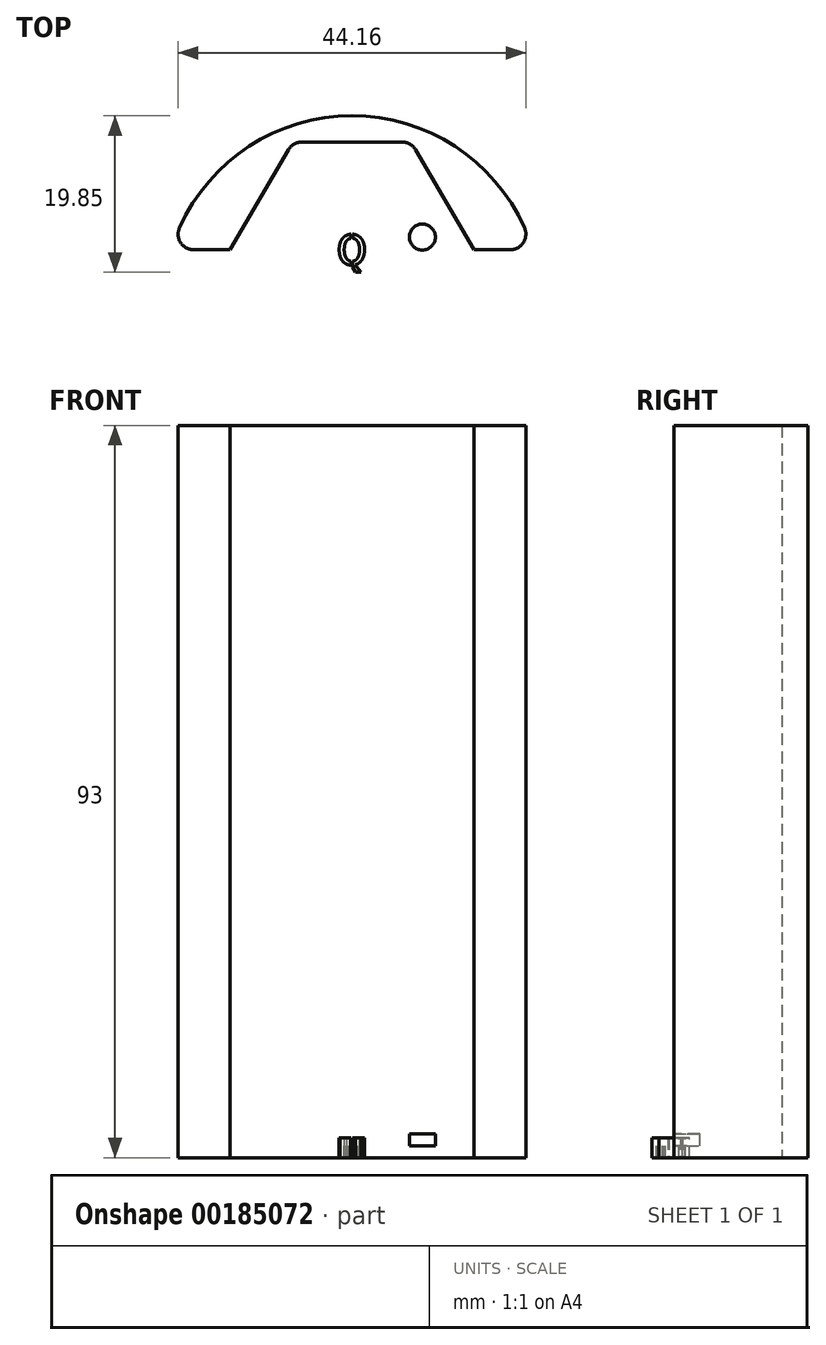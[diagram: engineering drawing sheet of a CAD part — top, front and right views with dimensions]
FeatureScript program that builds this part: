
annotation { "Feature Type Name" : "Feature", "Feature Type Description" : "" }
export const myFeature = defineFeature(function(context is Context, id is Id, definition is map)
    precondition{}
    {
        {
            var Q0;
            Q0=qCreatedBy(makeId("Top.planeOp"),FACE);
            var sketch = newSketch(context, id + "F0", { "sketchPlane" : qUnion([Q0])});
            skLineSegment(sketch, "E0", {"start": v(-15.5, -13.7) * mm, "end": v(-8.08, -1) * mm});
            skLineSegment(sketch, "E1", {"start": v(-6.35, 0) * mm, "end": v(6.35, 0) * mm});
            skLineSegment(sketch, "E2", {"start": v(8.08, -1) * mm, "end": v(15.5, -13.7) * mm});
            skLineSegment(sketch, "E3", {"start": v(-15.5, -13.7) * mm, "end": v(15.5, -13.7) * mm, "construction": true});
            skPoint(sketch, "E4", {"position": v(0, 0) * mm});
            skPoint(sketch, "E5", {"position": v(0, -13.7) * mm});
            skLineSegment(sketch, "E6", {"start": v(-15.5, -13.7) * mm, "end": v(-20.08, -13.7) * mm});
            skLineSegment(sketch, "E7", {"start": v(15.5, -13.7) * mm, "end": v(20.08, -13.7) * mm});
            skArc(sketch, "E8", {"start": v(21.9, -10.88) * mm, "mid": v(0, 3.32) * mm, "end": v(-21.9, -10.88) * mm});
            skPoint(sketch, "E9.visualSharp", {"position": v(-7.5, 0) * mm});
            skArc(sketch, "E9.filletArc", {"start": v(-6.35, 0) * mm, "mid": v(-7.35, -0.27) * mm, "end": v(-8.08, -1) * mm});
            skPoint(sketch, "E10.visualSharp", {"position": v(7.5, 0) * mm});
            skArc(sketch, "E10.filletArc", {"start": v(8.08, -1) * mm, "mid": v(7.35, -0.27) * mm, "end": v(6.35, 0) * mm});
            skPoint(sketch, "E11.visualSharp", {"position": v(-22.96, -13.7) * mm});
            skArc(sketch, "E11.filletArc", {"start": v(-21.9, -10.88) * mm, "mid": v(-21.76, -12.79) * mm, "end": v(-20.08, -13.7) * mm});
            skPoint(sketch, "E12.visualSharp", {"position": v(22.96, -13.7) * mm});
            skArc(sketch, "E12.filletArc", {"start": v(20.08, -13.7) * mm, "mid": v(21.76, -12.79) * mm, "end": v(21.9, -10.88) * mm});
            skSolve(sketch);
        }
        {
            var Q0;
            Q0=makeQuery(id+"F0.imprint","IMPRINT",FACE,{"disambiguationData":[TD([[makeQuery(id+"F0.imprint","IMPRINT",EDGE,{"derivedFrom":sQuery(id+"F0.wireOp",EDGE,"E0")}),1.0]])]});
            extrude(context, id + "F1", {"entities" : qUnion([Q0]), "depth" : 90 * mm});
        }
        {
            var Q0;
            Q0=makeQuery(id+"F1.opExtrude","CAP_FACE",FACE,{"disambiguationData":[OSD([sQuery(id+"F0.wireOp",EDGE,"E0"),sQuery(id+"F0.wireOp",EDGE,"E1"),sQuery(id+"F0.wireOp",EDGE,"E2"),sQuery(id+"F0.wireOp",EDGE,"E6"),sQuery(id+"F0.wireOp",EDGE,"E7"),sQuery(id+"F0.wireOp",EDGE,"E8"),sQuery(id+"F0.wireOp",EDGE,"E9.filletArc"),sQuery(id+"F0.wireOp",EDGE,"E10.filletArc")])],"isStart":true});
            var sketch = newSketch(context, id + "F2", { "sketchPlane" : qUnion([Q0])});
            skLineSegment(sketch, "E13", {"start": v(-17.96, 17.7) * mm, "end": v(17.96, 17.7) * mm});
            skArc(sketch, "E14", {"start": v(21.06, -6.01) * mm, "mid": v(0, -13.32) * mm, "end": v(-21.06, -6.01) * mm});
            skLineSegment(sketch, "E15", {"start": v(-22.96, -2.09) * mm, "end": v(-22.96, 12.7) * mm});
            skLineSegment(sketch, "E16", {"start": v(22.96, -2.09) * mm, "end": v(22.96, 12.7) * mm});
            skPoint(sketch, "E17.visualSharp", {"position": v(-22.96, 17.7) * mm});
            skArc(sketch, "E17.filletArc", {"start": v(-17.96, 17.7) * mm, "mid": v(-21.5, 16.24) * mm, "end": v(-22.96, 12.7) * mm});
            skPoint(sketch, "E18.visualSharp", {"position": v(22.96, 17.7) * mm});
            skArc(sketch, "E18.filletArc", {"start": v(22.96, 12.7) * mm, "mid": v(21.5, 16.24) * mm, "end": v(17.96, 17.7) * mm});
            skPoint(sketch, "E19.visualSharp", {"position": v(22.96, -4.4) * mm});
            skArc(sketch, "E19.filletArc", {"start": v(21.06, -6.01) * mm, "mid": v(22.46, -4.27) * mm, "end": v(22.96, -2.09) * mm});
            skPoint(sketch, "E20.visualSharp", {"position": v(-22.96, -4.4) * mm});
            skArc(sketch, "E20.filletArc", {"start": v(-22.96, -2.09) * mm, "mid": v(-22.46, -4.27) * mm, "end": v(-21.06, -6.01) * mm});
            skSolve(sketch);
        }
        {
            var Q0;
            Q0=makeQuery(id+"F2.imprint","IMPRINT",FACE,{"disambiguationData":[TD([[makeQuery(id+"F2.imprint","IMPRINT",EDGE,{"derivedFrom":sQuery(id+"F2.wireOp",EDGE,"E13")}),-1.0]])]});
            var Q1;
            Q1=makeQuery(id+"F0.imprint","IMPRINT",FACE,{"disambiguationData":[TD([[makeQuery(id+"F0.imprint","IMPRINT",EDGE,{"derivedFrom":sQuery(id+"F0.wireOp",EDGE,"E0")}),1.0]])]});
            extrude(context, id + "F3", {"entities" : qUnion([Q0, Q1]), "operationType" : NewBodyOperationType.ADD, "depth" : 3 * mm});
        }
        {
            var Q0;
            {var subQ0=sQuery(id+"F0.wireOp",EDGE,"E12.filletArc");var subQ1=sQuery(id+"F0.wireOp",EDGE,"E11.filletArc");var subQ2=sQuery(id+"F0.wireOp",EDGE,"E10.filletArc");var subQ3=sQuery(id+"F0.wireOp",EDGE,"E9.filletArc");var subQ4=sQuery(id+"F0.wireOp",EDGE,"E8");var subQ5=sQuery(id+"F0.wireOp",EDGE,"E7");var subQ6=sQuery(id+"F0.wireOp",EDGE,"E6");var subQ7=sQuery(id+"F0.wireOp",EDGE,"E2");var subQ8=sQuery(id+"F0.wireOp",EDGE,"E1");var subQ9=sQuery(id+"F0.wireOp",EDGE,"E0");Q0=makeQuery(id+"F3.boolean.opBoolean","MERGE",FACE,{"derivedFrom":[makeQuery(id+"F3.opExtrude","CAP_FACE",FACE,{"disambiguationData":[OSD([subQ9,subQ8,subQ7,subQ6,subQ5,subQ4,subQ3,subQ2,subQ1,subQ0])],"isStart":true}),makeQuery(id+"F3.opExtrude","CAP_FACE",FACE,{"disambiguationData":[OSD([subQ9,subQ8,subQ7,subQ6,subQ5,subQ4,subQ3,subQ2,subQ1,subQ0,sQuery(id+"F2.wireOp",EDGE,"E13"),sQuery(id+"F2.wireOp",EDGE,"E14"),sQuery(id+"F2.wireOp",EDGE,"a6c4aa1a-b442-44ca-937c-f53565c4f402.filletArc"),sQuery(id+"F2.wireOp",EDGE,"8f3339f9-6e3e-4ccb-8717-b49554667e36.filletArc")])],"isStart":true})]});}
            var sketch = newSketch(context, id + "F4", { "sketchPlane" : qUnion([Q0])});
            skCircle(sketch, "E21", {"center": v(0, -4.85) * mm, "radius": 1.65 * mm});
            skCircle(sketch, "E22", {"center": v(-8.94, -12.08) * mm, "radius": 1.65 * mm});
            skCircle(sketch, "E23.MirrorC", {"center": v(8.94, -12.08) * mm, "radius": 1.65 * mm});
            skText(sketch, "E24", { "text": "Q", "fontName": "AllertaStencil-Regular.ttf"});
            skPoint(sketch, "E25", {"position": v(0, -13.7) * mm});
            const initialGuessF4  = {"E24": [-0.00196, -0.01564, 1, 0, 0.00387]};
            skSetInitialGuess(sketch, initialGuessF4);
            skSolve(sketch);
        }
        {
            var Q0;
            Q0=makeQuery(id+"F4.imprint","IMPRINT",FACE,{"disambiguationData":[TD([[makeQuery(id+"F4.imprint","IMPRINT",EDGE,{"derivedFrom":sQuery(id+"F4.wireOp",EDGE,"E22")}),1.0]])]});
            var Q1;
            Q1=makeQuery(id+"F4.imprint","IMPRINT",FACE,{"disambiguationData":[TD([[makeQuery(id+"F4.imprint","IMPRINT",EDGE,{"derivedFrom":sQuery(id+"F4.wireOp",EDGE,"E21")}),1.0]])]});
            var Q2;
            Q2=makeQuery(id+"F4.imprint","IMPRINT",FACE,{"disambiguationData":[TD([[makeQuery(id+"F4.imprint","IMPRINT",EDGE,{"derivedFrom":sQuery(id+"F4.wireOp",EDGE,"E23.MirrorC")}),-1.0]])]});
            var Q3;
            {var subQ0=sQuery(id+"F0.wireOp",EDGE,"E12.filletArc");var subQ1=sQuery(id+"F0.wireOp",EDGE,"E11.filletArc");var subQ2=sQuery(id+"F0.wireOp",EDGE,"E10.filletArc");var subQ3=sQuery(id+"F0.wireOp",EDGE,"E9.filletArc");var subQ4=sQuery(id+"F0.wireOp",EDGE,"E8");var subQ5=sQuery(id+"F0.wireOp",EDGE,"E7");var subQ6=sQuery(id+"F0.wireOp",EDGE,"E6");var subQ7=sQuery(id+"F0.wireOp",EDGE,"E2");var subQ8=sQuery(id+"F0.wireOp",EDGE,"E1");var subQ9=sQuery(id+"F0.wireOp",EDGE,"E0");Q3=makeQuery(id+"F3.boolean.opBoolean","MERGE",FACE,{"derivedFrom":[makeQuery(id+"F3.opExtrude","CAP_FACE",FACE,{"disambiguationData":[OSD([subQ9,subQ8,subQ7,subQ6,subQ5,subQ4,subQ3,subQ2,subQ1,subQ0])],"isStart":false}),makeQuery(id+"F3.opExtrude","CAP_FACE",FACE,{"disambiguationData":[OSD([subQ9,subQ8,subQ7,subQ6,subQ5,subQ4,subQ3,subQ2,subQ1,subQ0,sQuery(id+"F2.wireOp",EDGE,"E13"),sQuery(id+"F2.wireOp",EDGE,"E14"),sQuery(id+"F2.wireOp",EDGE,"a6c4aa1a-b442-44ca-937c-f53565c4f402.filletArc"),sQuery(id+"F2.wireOp",EDGE,"8f3339f9-6e3e-4ccb-8717-b49554667e36.filletArc")])],"isStart":false})]});}
            extrude(context, id + "F5", {"entities" : qUnion([Q0, Q1, Q2]), "operationType" : NewBodyOperationType.REMOVE, "endBound" : BoundingType.UP_TO_SURFACE, "oppositeDirection" : true, "endBoundEntityFace" : qUnion([Q3]), "depth" : 25 * mm});
        }
        {
            var Q0;
            Q0=makeQuery(id+"F4.imprint","IMPRINT",FACE,{"disambiguationData":[TD([[makeQuery(id+"F4.imprint","IMPRINT",EDGE,{"derivedFrom":sQuery(id+"F4.wireOp",EDGE,"E24.sketch_text.stroke-0")}),-1.0]])]});
            var Q1;
            Q1=makeQuery(id+"F4.imprint","IMPRINT",FACE,{"disambiguationData":[TD([[makeQuery(id+"F4.imprint","IMPRINT",EDGE,{"derivedFrom":sQuery(id+"F4.wireOp",EDGE,"E24.sketch_text.stroke-19")}),-1.0]])]});
            extrude(context, id + "F6", {"entities" : qUnion([Q0, Q1]), "operationType" : NewBodyOperationType.REMOVE, "oppositeDirection" : true, "depth" : 0.5 * mm});
        }
        {
            var Q0;
            {var subQ0=sQuery(id+"F0.wireOp",EDGE,"E12.filletArc");var subQ1=sQuery(id+"F0.wireOp",EDGE,"E11.filletArc");var subQ2=sQuery(id+"F0.wireOp",EDGE,"E10.filletArc");var subQ3=sQuery(id+"F0.wireOp",EDGE,"E9.filletArc");var subQ4=sQuery(id+"F0.wireOp",EDGE,"E8");var subQ5=sQuery(id+"F0.wireOp",EDGE,"E7");var subQ6=sQuery(id+"F0.wireOp",EDGE,"E6");var subQ7=sQuery(id+"F0.wireOp",EDGE,"E2");var subQ8=sQuery(id+"F0.wireOp",EDGE,"E1");var subQ9=sQuery(id+"F0.wireOp",EDGE,"E0");Q0=makeQuery(id+"F3.boolean.opBoolean","MERGE",FACE,{"derivedFrom":[makeQuery(id+"F3.opExtrude","CAP_FACE",FACE,{"disambiguationData":[OSD([subQ9,subQ8,subQ7,subQ6,subQ5,subQ4,subQ3,subQ2,subQ1,subQ0])],"isStart":false}),makeQuery(id+"F3.opExtrude","CAP_FACE",FACE,{"disambiguationData":[OSD([subQ9,subQ8,subQ7,subQ6,subQ5,subQ4,subQ3,subQ2,subQ1,subQ0,sQuery(id+"F2.wireOp",EDGE,"E13"),sQuery(id+"F2.wireOp",EDGE,"E14"),sQuery(id+"F2.wireOp",EDGE,"a6c4aa1a-b442-44ca-937c-f53565c4f402.filletArc"),sQuery(id+"F2.wireOp",EDGE,"8f3339f9-6e3e-4ccb-8717-b49554667e36.filletArc")])],"isStart":false})]});}
            var sketch = newSketch(context, id + "F7", { "sketchPlane" : qUnion([Q0])});
            skCircle(sketch, "E26", {"center": v(-8.94, 12.08) * mm, "radius": 2.9 * mm});
            skCircle(sketch, "E27", {"center": v(0, 4.85) * mm, "radius": 2.9 * mm});
            skCircle(sketch, "E28", {"center": v(8.94, 12.08) * mm, "radius": 2.9 * mm});
            skSolve(sketch);
        }
        {
            var Q0;
            Q0 = qSketchRegion(id + "F7", true);
            extrude(context, id + "F8", {"entities" : qUnion([Q0]), "operationType" : NewBodyOperationType.REMOVE, "oppositeDirection" : true, "depth" : 1.5 * mm});
        }
    });
